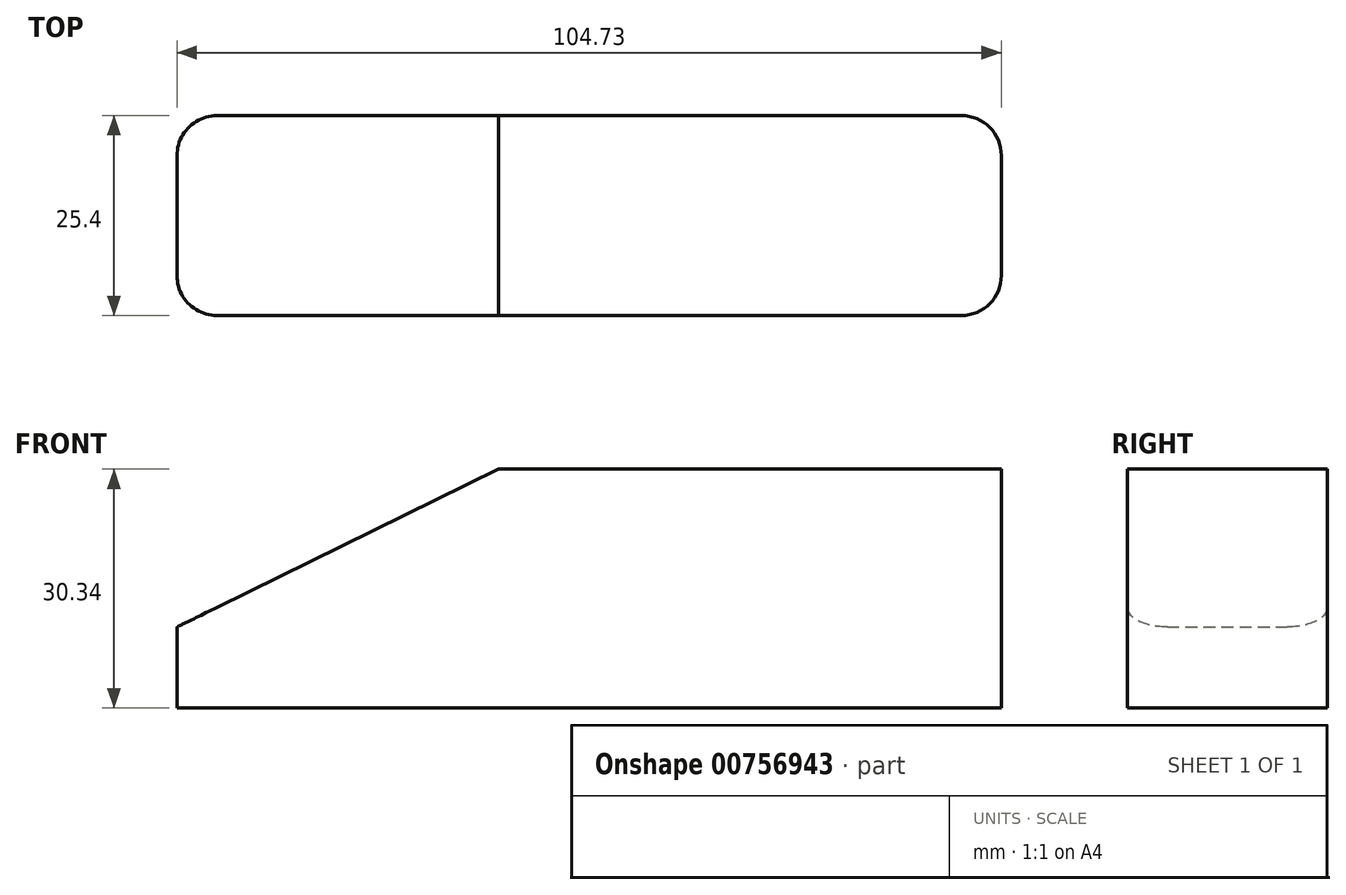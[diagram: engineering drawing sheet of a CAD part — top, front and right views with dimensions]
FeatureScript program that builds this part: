
annotation { "Feature Type Name" : "Feature", "Feature Type Description" : "" }
export const myFeature = defineFeature(function(context is Context, id is Id, definition is map)
    precondition{}
    {
        {
            var Q0;
            Q0=qCreatedBy(makeId("Front.planeOp"),FACE);
            var sketch = newSketch(context, id + "F0", { "sketchPlane" : qUnion([Q0])});
            skLineSegment(sketch, "E0", {"start": v(-57.87, 14.8) * mm, "end": v(-17, 34.87) * mm});
            skLineSegment(sketch, "E1", {"start": v(-17, 34.87) * mm, "end": v(46.86, 34.87) * mm});
            skLineSegment(sketch, "E2", {"start": v(46.86, 34.87) * mm, "end": v(46.86, 4.53) * mm});
            skLineSegment(sketch, "E3", {"start": v(46.86, 4.53) * mm, "end": v(-57.87, 4.53) * mm});
            skLineSegment(sketch, "E4", {"start": v(-57.87, 4.53) * mm, "end": v(-57.87, 14.8) * mm});
            skLineSegment(sketch, "E5", {"start": v(-57.87, 9.66) * mm, "end": v(-57.87, 14.8) * mm});
            skSolve(sketch);
        }
        {
            var Q0;
            {var subQ1=sQuery(id+"F0.wireOp",EDGE,"E0");Q0=makeQuery(id+"F0.imprint","IMPRINT",FACE,{"disambiguationData":[TD([[makeQuery(id+"F0.imprint","IMPRINT",EDGE,{"derivedFrom":subQ1}),-1.0]])]});}
            extrude(context, id + "F1", {"entities" : qUnion([Q0]), "depth" : 25.4 * mm, "offsetDistance" : 25.4 * mm});
        }
        {
            var Q0;
            Q0=makeQuery(id+"F1.opExtrude","CAP_EDGE",EDGE,{"disambiguationData":[OSD([sQuery(id+"F0.wireOp",EDGE,"E4")])],"isStart":false});
            var Q1;
            Q1=makeQuery(id+"F1.opExtrude","CAP_EDGE",EDGE,{"disambiguationData":[OSD([sQuery(id+"F0.wireOp",EDGE,"E4")])],"isStart":true});
            var Q2;
            Q2=makeQuery(id+"F1.opExtrude","CAP_EDGE",EDGE,{"disambiguationData":[OSD([sQuery(id+"F0.wireOp",EDGE,"E2")])],"isStart":false});
            var Q3;
            Q3=makeQuery(id+"F1.opExtrude","CAP_EDGE",EDGE,{"disambiguationData":[OSD([sQuery(id+"F0.wireOp",EDGE,"E2")])],"isStart":true});
            fillet(context, id + "F2", {"entities" : qUnion([Q0, Q1, Q2, Q3]), "radius" : 5.08 * mm, "tangentPropagation" : true, "allowEdgeOverflow" : false});
        }
    });
